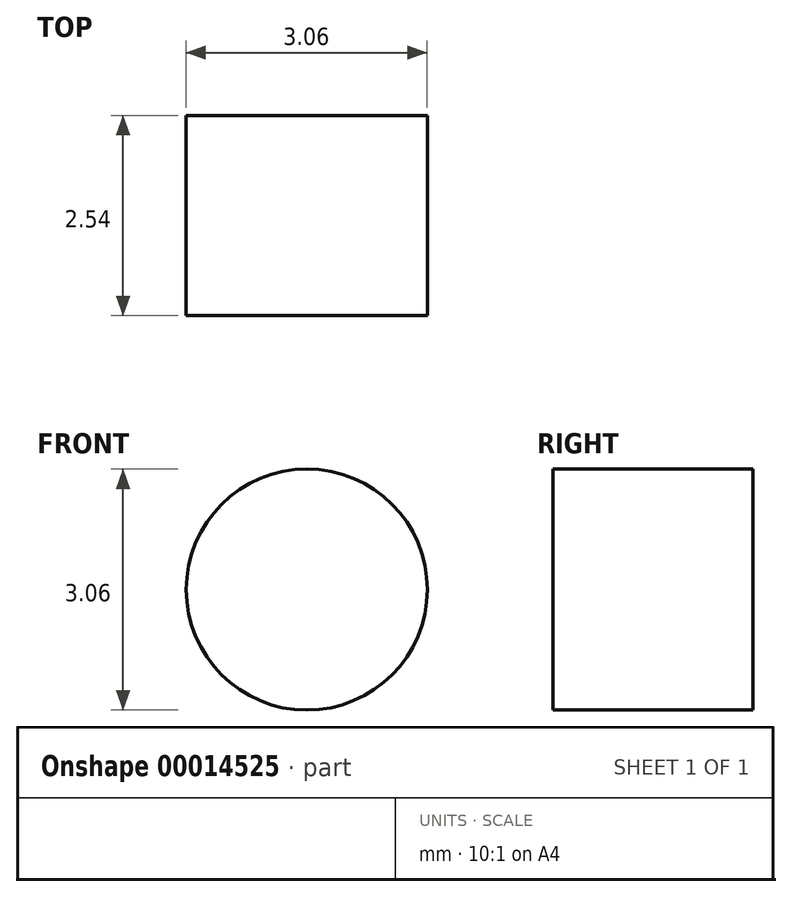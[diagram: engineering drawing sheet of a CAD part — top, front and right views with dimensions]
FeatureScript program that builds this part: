
annotation { "Feature Type Name" : "Feature", "Feature Type Description" : "" }
export const myFeature = defineFeature(function(context is Context, id is Id, definition is map)
    precondition{}
    {
        {
            var Q0;
            Q0=qCreatedBy(makeId("Front.planeOp"),FACE);
            var sketch = newSketch(context, id + "F0", { "sketchPlane" : qUnion([Q0])});
            skCircle(sketch, "E0", {"center": v(0, 0) * mm, "radius": 1.53 * mm});
            skCircle(sketch, "E1", {"center": v(55.05, 26.93) * mm, "radius": 1.53 * mm});
            skSolve(sketch);
        }
        {
            var Q0;
            Q0=makeQuery(id+"F0.imprint","IMPRINT",FACE,{"disambiguationData":[TD([[makeQuery(id+"F0.imprint","IMPRINT",EDGE,{"derivedFrom":sQuery(id+"F0.wireOp",EDGE,"E1")}),1.0]])]});
            extrude(context, id + "F1", {"entities" : qUnion([Q0]), "depth" : 2.54 * mm});
        }
    });
